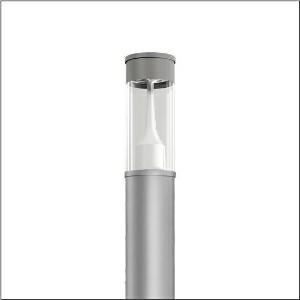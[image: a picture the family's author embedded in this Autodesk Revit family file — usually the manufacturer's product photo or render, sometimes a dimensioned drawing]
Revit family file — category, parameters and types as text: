
# Revit family: city-light_260_iq___pl1_2s_5xa5295jf14h_6623
name_source: partatom
category: Lighting Fixtures
units: mm (PartAtom-declared; Revit-internal decimal feet)

## family parameters
Cut with Voids When Loaded = No
Host = Face
Light Source = No
Part Type = Normal
Room Calculation Point = No
Round Connector Dimension = Use Diameter
Shared = No

## types (1)
- --- (1 x LED, 2970 lm, 19.3 W, 3000K)
    Apparent Load = 19 VA
    CIE Flux Codes = 23 62 94 96 100
    Color Rendering = 70
    Color Temperature = 3000K
    Default Elevation = 1800 mm
    Description = City-Light 260 iQ, light pillar, Module 540 iQ-SR, primary light control with 3 zone facetted reflector, of plastic, silver coated, highly specular, structured, primary optical cover: cover, of PMMA, transparent, light distribution: PL1.2s, primary light characteristic: symmetric, LED, High Power LED, rated luminous flux: 2.970lm, luminous efficacy: 154lm/W, light colour: 730, colour temperature: 3000K, control gear: iQ Street-Remote, control: Auto-Match, Temp-Guard, Lumen-Switch, Night-Set, Smart-Wire, Light-Fading, Desk-Remote (wireless, voltage-free reading and setting of iQ features in the workshop via application-optimized NFC function/RFID function), optimised constant luminous flux control (CLO 2.0), Street-Remote, pre-setting: logarithmic dimming characteristic, with terminal, 6-pole, max. 2.5mm², mains connection: 230..240V, AC, 50/60Hz, start of lifetime: 19W, end of service life: 21W, reduction: 10W, luminaire housing, cylindrical, of extruded aluminium section, coated, Siteco® metallic grey (DB 702S), length: 2.600mm, diameter: 200mm, Module 540 iQ-SR, traffic white (RAL 9016), equipment: standard, protection rating (complete): IP65, insulation class (complete): insulation class II (safety insulation), certification: CE, ENEC, VDE, packaging unit: 1 piece

Light Distribution: PL1.2s
    Height = 500 mm
    Lamp = 1 x LED
    Lamp Light Flux = 2970 lm
    Lamp Power = 19.3 W
    Lamp count = 1
    Length = 200 mm  [stored 0.656168 ft]
    Luminous efficacy = 154 lm/W
    Manufacturer = Siteco
    ModVariant = No
    Model = 5XA5295JF14H
    Mounting Place = Floor
    Mounting Type = Freestanding
    Number of Poles = 1
    OnlyDefault = Yes
    Power Factor = 1
    Product Name = City-Light 260 iQ | PL1.2s
    Product group = light pillar
    ProductGroupID = 1301
    Protection Class = Protection class II
    Protection Degree = IP 65
    RLX_Detail_Level = 1
    RLX_Emergency_Light_Flux = 0 lm
    RLX_Emergency_Type = 0
    RLX_Emergency_Type_DB = No
    RlxData = <blob elided: 21873 chars, md5=7839012c>
    Socket = socket
    Standby Power = 0 W
    System Light Flux = 2970 lm
    System Power = 19 W
    Type Comments = factory setting: luminous flux: 100 % | dim-lin: 254 | 403 mA
    Type Image = l_1006920.jpg
    URL = http://relux.com
    VarID = @adj_053099
    Voltage = 0 V
    Weight = 0.00 kg
    Width = 0 mm  [stored 0 ft]

note: [stored X ft] marks values corroborated as IEEE doubles in the binary element streams (Revit-internal decimal feet)

## geometry (parser evidence)
native form markers: Blend x4, Sweep x10
no freeform markers — native parametric forms only
